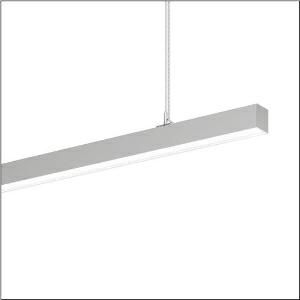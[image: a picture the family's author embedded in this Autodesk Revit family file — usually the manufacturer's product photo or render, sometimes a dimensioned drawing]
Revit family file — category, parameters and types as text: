
# Revit family: silica_r__21_51mx30da44sb_e9ec
name_source: partatom
category: Lighting Fixtures
units: mm (PartAtom-declared; Revit-internal decimal feet)

## family parameters
Cut with Voids When Loaded = No
Host = Face
Light Source = No
Part Type = Normal
Room Calculation Point = No
Round Connector Dimension = Use Diameter
Shared = No

## types (1)
- --- (1 x LED, 4210 lm, 26 W, 4000K)
    Apparent Load = 26 VA
    CIE Flux Codes = 47 79 96 57 100
    Color Rendering = 80
    Color Temperature = 4000K
    Default Elevation = 1800 mm
    Description = Silica® 21, office luminaire, primary optical cover: cover, of PMMA, opal, light emission: direct/indirect distribution, primary light characteristic: symmetric, installation type: suspended mounting, LED, rated luminous flux: 4.210lm, luminous efficacy: 162lm/W, light colour: 840, colour temperature: 4000K, with terminal, 3+2-pole, max. 2.5mm², mains connection: 220..240V, AC, 50/60Hz, rated input power: 26W, luminaire housing, of aluminium, metallic grey (RAL 9006), length: 1.204mm, width: 53mm, height: 53mm, protection rating (complete): IP20, insulation class (complete): insulation class I (protective earthing), certification: CE, permissible operating ambient temperature: 0..+35°C, standard: EN 50419, packaging unit: 1 piece
    Height = 53 mm
    Lamp = 1 x LED
    Lamp Light Flux = 4210 lm
    Lamp Power = 26 W
    Lamp count = 1
    Length = 1204 mm
    Luminous efficacy = 162 lm/W
    Manufacturer = Siteco
    ModVariant = No
    Model = 51MX30DA44SB
    Mounting Place = Ceiling
    Mounting Type = Pendant
    Number of Poles = 1
    OnlyDefault = Yes
    Power Factor = 1
    Product Name = Silica® 21
    Product group = office luminaire | ceiling pendant
    ProductGroupID = 902
    Protection Class = Protection class I
    Protection Degree = IP 20
    RLX_Detail_Level = 1
    RLX_Emergency_Light_Flux = 0 lm
    RLX_Emergency_Type = 0
    RLX_Emergency_Type_DB = No
    RlxData = <blob elided: 23169 chars, md5=46c3274a>
    Socket = socket
    Standby Power = 0 W
    System Light Flux = 4210 lm
    System Power = 26 W
    Type Comments = factory setting: luminous flux: 100 % | dim-lin: 254 | 218 mA
    Type Image = l_1335864.jpg
    URL = http://relux.com
    VarID = @adj_086033
    Voltage = 0 V
    Weight = 0.00 kg
    Width = 53 mm

## geometry (parser evidence)
native form markers: Blend x4, Sweep x12
no freeform markers — native parametric forms only
